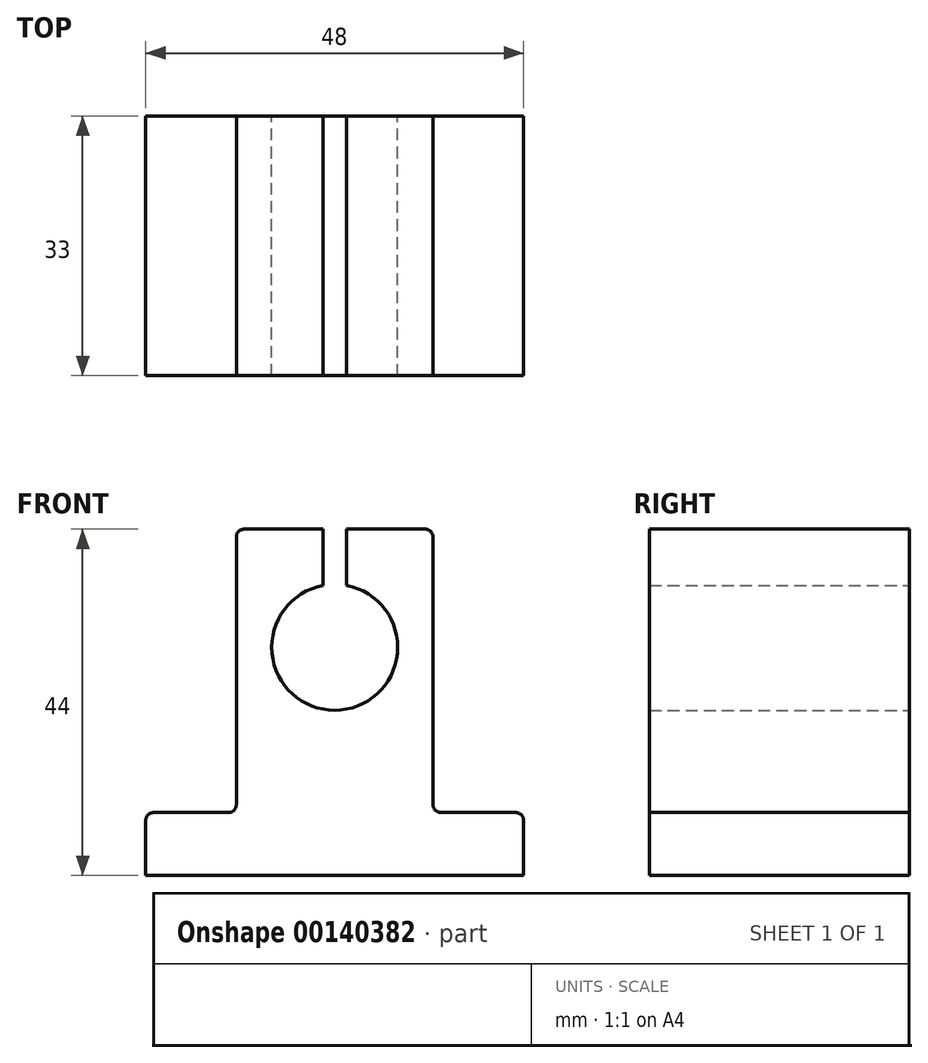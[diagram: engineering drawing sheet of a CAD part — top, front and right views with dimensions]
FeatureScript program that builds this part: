
annotation { "Feature Type Name" : "Feature", "Feature Type Description" : "" }
export const myFeature = defineFeature(function(context is Context, id is Id, definition is map)
    precondition{}
    {
        {
            var Q0;
            Q0=qCreatedBy(makeId("Front.planeOp"),FACE);
            var sketch = newSketch(context, id + "F0", { "sketchPlane" : qUnion([Q0])});
            skLineSegment(sketch, "E0", {"start": v(-24, -19.36) * mm, "end": v(24, -19.36) * mm});
            skLineSegment(sketch, "E1", {"start": v(24, -19.36) * mm, "end": v(24, -12.36) * mm});
            skLineSegment(sketch, "E2", {"start": v(-24, -19.36) * mm, "end": v(-24, -12.36) * mm});
            skLineSegment(sketch, "E3", {"start": v(-23, -11.36) * mm, "end": v(-13.5, -11.36) * mm});
            skLineSegment(sketch, "E4", {"start": v(23, -11.36) * mm, "end": v(13.5, -11.36) * mm});
            skLineSegment(sketch, "E5", {"start": v(12.5, -10.36) * mm, "end": v(12.5, 23.64) * mm});
            skLineSegment(sketch, "E6", {"start": v(-12.5, -10.36) * mm, "end": v(-12.5, 23.64) * mm});
            skLineSegment(sketch, "E7", {"start": v(-11.5, 24.64) * mm, "end": v(-1.5, 24.64) * mm});
            skLineSegment(sketch, "E8", {"start": v(0, 9.64) * mm, "end": v(0, -11.47) * mm, "construction": true});
            skPoint(sketch, "E9.visualSharp", {"position": v(-12.5, 24.64) * mm});
            skArc(sketch, "E9.filletArc", {"start": v(-11.5, 24.64) * mm, "mid": v(-12.2, 24.35) * mm, "end": v(-12.5, 23.64) * mm});
            skPoint(sketch, "E10.visualSharp", {"position": v(12.5, 24.64) * mm});
            skArc(sketch, "E10.filletArc", {"start": v(12.5, 23.64) * mm, "mid": v(12.2, 24.35) * mm, "end": v(11.5, 24.64) * mm});
            skPoint(sketch, "E11.visualSharp", {"position": v(24, -11.36) * mm});
            skArc(sketch, "E11.filletArc", {"start": v(24, -12.36) * mm, "mid": v(23.7, -11.65) * mm, "end": v(23, -11.36) * mm});
            skPoint(sketch, "E12.visualSharp", {"position": v(-24, -11.36) * mm});
            skArc(sketch, "E12.filletArc", {"start": v(-23, -11.36) * mm, "mid": v(-23.7, -11.65) * mm, "end": v(-24, -12.36) * mm});
            skPoint(sketch, "E13.visualSharp", {"position": v(-12.5, -11.36) * mm});
            skArc(sketch, "E13.filletArc", {"start": v(-13.5, -11.36) * mm, "mid": v(-12.8, -11.06) * mm, "end": v(-12.5, -10.36) * mm});
            skPoint(sketch, "E14.visualSharp", {"position": v(12.5, -11.36) * mm});
            skArc(sketch, "E14.filletArc", {"start": v(12.5, -10.36) * mm, "mid": v(12.8, -11.06) * mm, "end": v(13.5, -11.36) * mm});
            skArc(sketch, "E15", {"start": v(-1.5, 17.5) * mm, "mid": v(0, 1.64) * mm, "end": v(1.5, 17.5) * mm});
            skLineSegment(sketch, "E16", {"start": v(-1.5, 17.5) * mm, "end": v(-1.5, 24.64) * mm});
            skLineSegment(sketch, "E17.MirrorCS", {"start": v(1.5, 17.5) * mm, "end": v(1.5, 24.64) * mm});
            skPoint(sketch, "E18.orphan", {"position": v(-1.5, 35.94) * mm});
            skPoint(sketch, "E19.orphan", {"position": v(1.5, 35.94) * mm});
            skPoint(sketch, "E20.orphan", {"position": v(-1.5, 9.64) * mm});
            skPoint(sketch, "E21.orphan", {"position": v(1.5, 9.64) * mm});
            skLineSegment(sketch, "E22.trimOffspring", {"start": v(1.5, 24.64) * mm, "end": v(11.5, 24.64) * mm});
            skPoint(sketch, "E23.orphan", {"position": v(0, 21.1) * mm});
            skSolve(sketch);
        }
        {
            var Q0;
            Q0 = qSketchRegion(id + "F0", true);
            extrude(context, id + "F1", {"entities" : qUnion([Q0]), "endBound" : BoundingType.SYMMETRIC, "depth" : 16 * mm});
        }
        {
            var Q0;
            Q0 = qSketchRegion(id + "F0", true);
            extrude(context, id + "F2", {"entities" : qUnion([Q0]), "operationType" : NewBodyOperationType.ADD, "depth" : 25 * mm});
        }
    });
